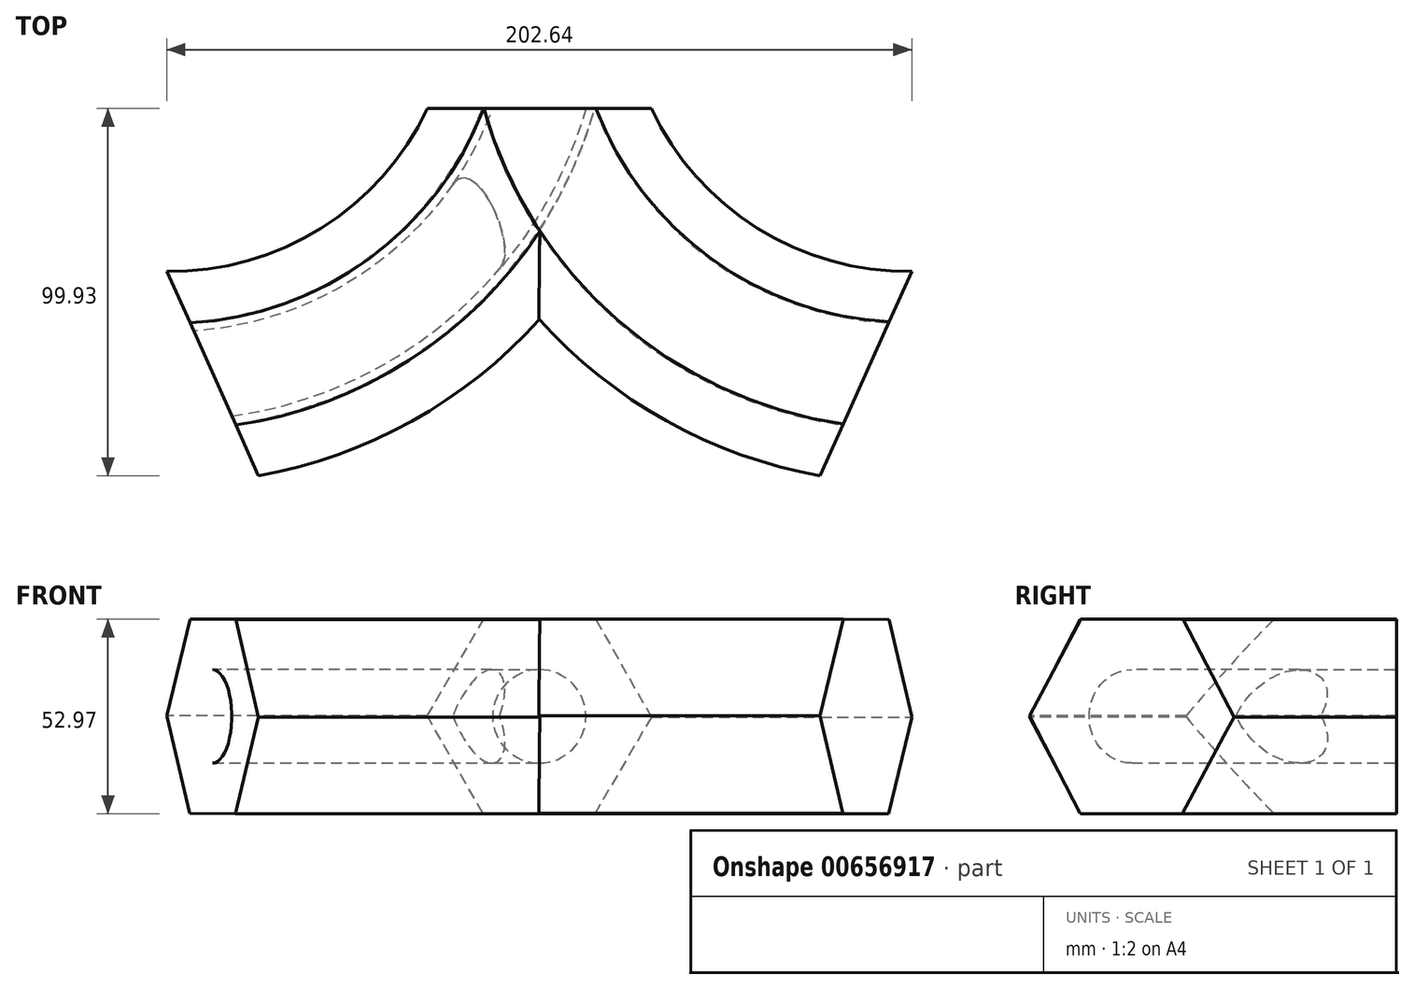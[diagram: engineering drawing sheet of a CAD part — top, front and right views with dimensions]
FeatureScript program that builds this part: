
annotation { "Feature Type Name" : "Feature", "Feature Type Description" : "" }
export const myFeature = defineFeature(function(context is Context, id is Id, definition is map)
    precondition{}
    {
        {
            var Q0;
            Q0=qCreatedBy(makeId("Front.planeOp"),FACE);
            var sketch = newSketch(context, id + "F0", { "sketchPlane" : qUnion([Q0])});
            skCircle(sketch, "E0.cCircle", {"center": v(0, 26.89) * mm, "radius": 26.4 * mm, "construction": true});
            skLineSegment(sketch, "E0.0", {"start": v(-15.4, 0.58) * mm, "end": v(-30.48, 27.07) * mm});
            skLineSegment(sketch, "E0.1", {"start": v(-30.48, 27.07) * mm, "end": v(-15.08, 53.37) * mm});
            skLineSegment(sketch, "E0.2", {"start": v(-15.08, 53.37) * mm, "end": v(15.4, 53.2) * mm});
            skLineSegment(sketch, "E0.3", {"start": v(15.4, 53.2) * mm, "end": v(30.48, 26.7) * mm});
            skLineSegment(sketch, "E0.4", {"start": v(30.48, 26.7) * mm, "end": v(15.08, 0.4) * mm});
            skLineSegment(sketch, "E0.5", {"start": v(15.08, 0.4) * mm, "end": v(-15.4, 0.58) * mm});
            skPoint(sketch, "E0.0.midPoint", {"position": v(-22.94, 13.82) * mm});
            skCircle(sketch, "E1", {"center": v(0, 26.89) * mm, "radius": 12.7 * mm});
            skSolve(sketch);
        }
        {
            var Q0;
            Q0=qCreatedBy(makeId("Top.planeOp"),FACE);
            var sketch = newSketch(context, id + "F1", { "sketchPlane" : qUnion([Q0])});
            skArc(sketch, "E2", {"start": v(-88.86, -72.11) * mm, "mid": v(-33.77, -49.2) * mm, "end": v(0, 0) * mm});
            skArc(sketch, "E3.MirrorCS", {"start": v(88.86, -72.11) * mm, "mid": v(33.77, -49.2) * mm, "end": v(0, 0) * mm});
            skSolve(sketch);
        }
        {
            var Q0;
            Q0=makeQuery(id+"F0.imprint","IMPRINT",FACE,{"disambiguationData":[TD([[makeQuery(id+"F0.imprint","IMPRINT",EDGE,{"derivedFrom":sQuery(id+"F0.wireOp",EDGE,"E0.0")}),-1.0]])]});
            var Q1;
            Q1=sQuery(id+"F1.wireOp",EDGE,"E2");
            sweep(context, id + "F2", {"profiles" : qUnion([Q0]), "path" : qUnion([Q1])});
        }
        {
            var Q0;
            Q0=makeQuery(id+"F0.imprint","IMPRINT",FACE,{"disambiguationData":[TD([[makeQuery(id+"F0.imprint","IMPRINT",EDGE,{"derivedFrom":sQuery(id+"F0.wireOp",EDGE,"E1")}),1.0]])]});
            var Q1;
            Q1=makeQuery(id+"F0.imprint","IMPRINT",FACE,{"disambiguationData":[TD([[makeQuery(id+"F0.imprint","IMPRINT",EDGE,{"derivedFrom":sQuery(id+"F0.wireOp",EDGE,"E0.0")}),-1.0]])]});
            var Q2;
            Q2=sQuery(id+"F1.wireOp",EDGE,"E3.MirrorCS");
            sweep(context, id + "F3", {"operationType" : NewBodyOperationType.ADD, "profiles" : qUnion([Q0, Q1]), "path" : qUnion([Q2])});
        }
        {
            var Q0;
            Q0=makeQuery(id+"F0.imprint","IMPRINT",FACE,{"disambiguationData":[TD([[makeQuery(id+"F0.imprint","IMPRINT",EDGE,{"derivedFrom":sQuery(id+"F0.wireOp",EDGE,"E1")}),1.0]])]});
            var Q1;
            Q1=sQuery(id+"F1.wireOp",EDGE,"E2");
            sweep(context, id + "F4", {"operationType" : NewBodyOperationType.REMOVE, "profiles" : qUnion([Q0]), "path" : qUnion([Q1])});
        }
    });
